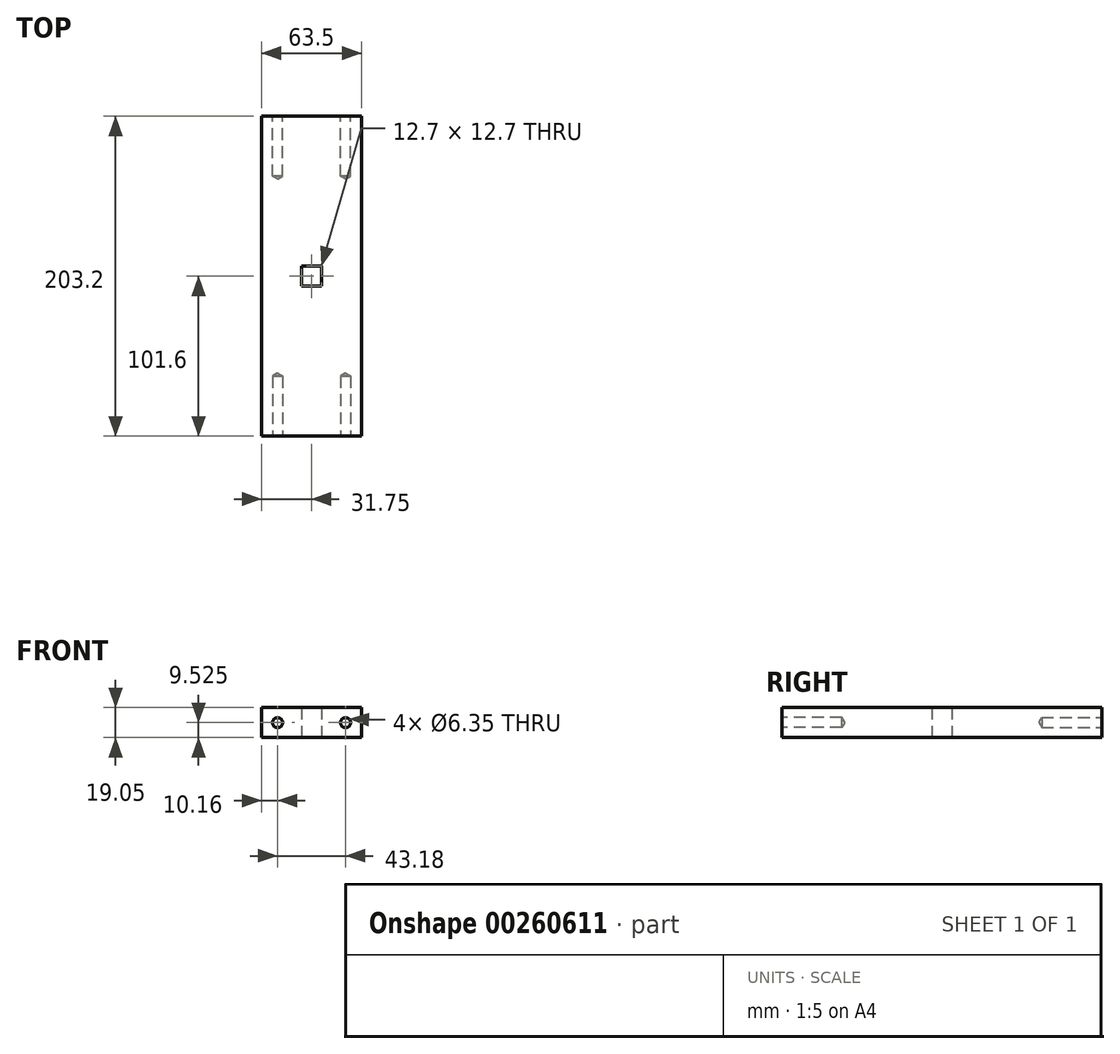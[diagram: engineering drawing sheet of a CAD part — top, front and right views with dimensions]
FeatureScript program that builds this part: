
annotation { "Feature Type Name" : "Feature", "Feature Type Description" : "" }
export const myFeature = defineFeature(function(context is Context, id is Id, definition is map)
    precondition{}
    {
        {
            var Q0;
            Q0=qCreatedBy(makeId("Top.planeOp"),FACE);
            var sketch = newSketch(context, id + "F0", { "sketchPlane" : qUnion([Q0])});
            skLineSegment(sketch, "E0.bottom", {"start": v(31.75, -101.6) * mm, "end": v(-31.75, -101.6) * mm});
            skLineSegment(sketch, "E0.top", {"start": v(31.75, 101.6) * mm, "end": v(-31.75, 101.6) * mm});
            skLineSegment(sketch, "E0.left", {"start": v(31.75, -101.6) * mm, "end": v(31.75, 101.6) * mm});
            skLineSegment(sketch, "E0.right", {"start": v(-31.75, -101.6) * mm, "end": v(-31.75, 101.6) * mm});
            skPoint(sketch, "E0.middle", {"position": v(0, 0) * mm});
            skLineSegment(sketch, "E1.bottom", {"start": v(6.35, 6.35) * mm, "end": v(-6.35, 6.35) * mm});
            skLineSegment(sketch, "E1.top", {"start": v(6.35, -6.35) * mm, "end": v(-6.35, -6.35) * mm});
            skLineSegment(sketch, "E1.left", {"start": v(6.35, 6.35) * mm, "end": v(6.35, -6.35) * mm});
            skLineSegment(sketch, "E1.right", {"start": v(-6.35, 6.35) * mm, "end": v(-6.35, -6.35) * mm});
            skSolve(sketch);
        }
        {
            var Q0;
            Q0=makeQuery(id+"F0.imprint","IMPRINT",FACE,{"disambiguationData":[TD([[makeQuery(id+"F0.imprint","IMPRINT",EDGE,{"derivedFrom":sQuery(id+"F0.wireOp",EDGE,"E0.bottom")}),-1.0]])]});
            extrude(context, id + "F1", {"entities" : qUnion([Q0]), "depth" : 19.05 * mm});
        }
        {
            var Q0;
            Q0=makeQuery(id+"F1.opExtrude","SWEPT_FACE",FACE,{"disambiguationData":[OSD([sQuery(id+"F0.wireOp",EDGE,"E0.bottom")])]});
            var sketch = newSketch(context, id + "F2", { "sketchPlane" : qUnion([Q0])});
            skPoint(sketch, "E2", {"position": v(21.59, 9.53) * mm});
            skPoint(sketch, "E3", {"position": v(-21.6, 9.53) * mm});
            skSolve(sketch);
        }
        {
            var Q0;
            Q0=sQuery(id+"F2.wireOp",VERTEX,"E3");
            var Q1;
            Q1=sQuery(id+"F2.wireOp",VERTEX,"E2");
            var Q2;
            Q2=makeQuery(id+"F1.opExtrude","SWEPT_BODY",BODY,{"disambiguationData":[OSD([sQuery(id+"F0.wireOp",EDGE,"E0.bottom"),sQuery(id+"F0.wireOp",EDGE,"E0.top"),sQuery(id+"F0.wireOp",EDGE,"E0.left"),sQuery(id+"F0.wireOp",EDGE,"E0.right"),sQuery(id+"F0.wireOp",EDGE,"E1.bottom"),sQuery(id+"F0.wireOp",EDGE,"E1.top"),sQuery(id+"F0.wireOp",EDGE,"E1.left"),sQuery(id+"F0.wireOp",EDGE,"E1.right")])]});
            hole(context, id + "F3", {"style" : HoleStyle.SIMPLE, "endStyle" : HoleEndStyle.BLIND, "holeDiameter" : 6.35 * mm, "holeDepth" : 38.1 * mm, "tappedDepth" : 12.7 * mm, "tapClearance" : 3, "locations" : qUnion([Q0, Q1]), "scope" : qUnion([Q2])});
        }
        {
            var Q0;
            Q0=makeQuery(id+"F1.opExtrude","SWEPT_FACE",FACE,{"disambiguationData":[OSD([sQuery(id+"F0.wireOp",EDGE,"E0.top")])]});
            var sketch = newSketch(context, id + "F4", { "sketchPlane" : qUnion([Q0])});
            skPoint(sketch, "E4", {"position": v(21.59, 9.53) * mm});
            skPoint(sketch, "E5", {"position": v(-21.6, 9.52) * mm});
            skSolve(sketch);
        }
        {
            var Q0;
            Q0=sQuery(id+"F4.wireOp",VERTEX,"E4");
            var Q1;
            Q1=sQuery(id+"F4.wireOp",VERTEX,"E5");
            var Q2;
            Q2=makeQuery(id+"F1.opExtrude","SWEPT_BODY",BODY,{"disambiguationData":[OSD([sQuery(id+"F0.wireOp",EDGE,"E0.bottom"),sQuery(id+"F0.wireOp",EDGE,"E0.top"),sQuery(id+"F0.wireOp",EDGE,"E0.left"),sQuery(id+"F0.wireOp",EDGE,"E0.right"),sQuery(id+"F0.wireOp",EDGE,"E1.bottom"),sQuery(id+"F0.wireOp",EDGE,"E1.top"),sQuery(id+"F0.wireOp",EDGE,"E1.left"),sQuery(id+"F0.wireOp",EDGE,"E1.right")])]});
            hole(context, id + "F5", {"style" : HoleStyle.SIMPLE, "endStyle" : HoleEndStyle.BLIND, "holeDiameter" : 6.35 * mm, "holeDepth" : 38.1 * mm, "tappedDepth" : 12.7 * mm, "tapClearance" : 3, "locations" : qUnion([Q0, Q1]), "scope" : qUnion([Q2])});
        }
    });
